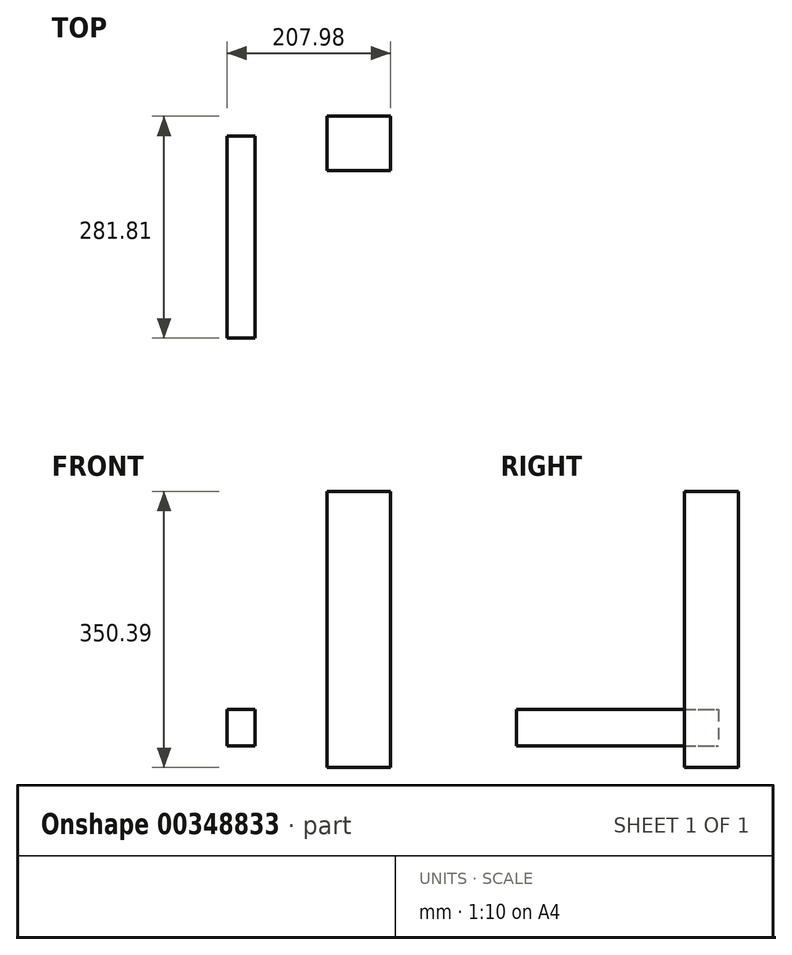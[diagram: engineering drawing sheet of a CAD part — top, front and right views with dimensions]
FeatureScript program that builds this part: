
annotation { "Feature Type Name" : "Feature", "Feature Type Description" : "" }
export const myFeature = defineFeature(function(context is Context, id is Id, definition is map)
    precondition{}
    {
        {
            var Q0;
            Q0=qCreatedBy(makeId("Front.planeOp"),FACE);
            var sketch = newSketch(context, id + "F0", { "sketchPlane" : qUnion([Q0])});
            skLineSegment(sketch, "E0.bottom", {"start": v(-67.55, 73.27) * mm, "end": v(-31.9, 73.27) * mm});
            skLineSegment(sketch, "E0.top", {"start": v(-67.55, 27.5) * mm, "end": v(-31.9, 27.5) * mm});
            skLineSegment(sketch, "E0.left", {"start": v(-67.55, 73.27) * mm, "end": v(-67.55, 27.5) * mm});
            skLineSegment(sketch, "E0.right", {"start": v(-31.9, 73.27) * mm, "end": v(-31.9, 27.5) * mm});
            skSolve(sketch);
        }
        {
            var Q0;
            Q0=makeQuery(id+"F0.imprint","IMPRINT",FACE,{"disambiguationData":[TD([[makeQuery(id+"F0.imprint","IMPRINT",EDGE,{"derivedFrom":sQuery(id+"F0.wireOp",EDGE,"E0.bottom")}),-1.0]])]});
            extrude(context, id + "F1", {"entities" : qUnion([Q0]), "depth" : 256.64 * mm});
        }
        {
            var Q0;
            Q0=qCreatedBy(makeId("Top.planeOp"),FACE);
            var sketch = newSketch(context, id + "F2", { "sketchPlane" : qUnion([Q0])});
            skLineSegment(sketch, "E1.bottom", {"start": v(59.62, 25.17) * mm, "end": v(140.43, 25.17) * mm});
            skLineSegment(sketch, "E1.top", {"start": v(59.62, -43.67) * mm, "end": v(140.43, -43.67) * mm});
            skLineSegment(sketch, "E1.left", {"start": v(59.62, 25.17) * mm, "end": v(59.62, -43.67) * mm});
            skLineSegment(sketch, "E1.right", {"start": v(140.43, 25.17) * mm, "end": v(140.43, -43.67) * mm});
            skSolve(sketch);
        }
        {
            var Q0;
            Q0 = qSketchRegion(id + "F2", true);
            extrude(context, id + "F3", {"entities" : qUnion([Q0]), "depth" : 350.4 * mm});
        }
    });
